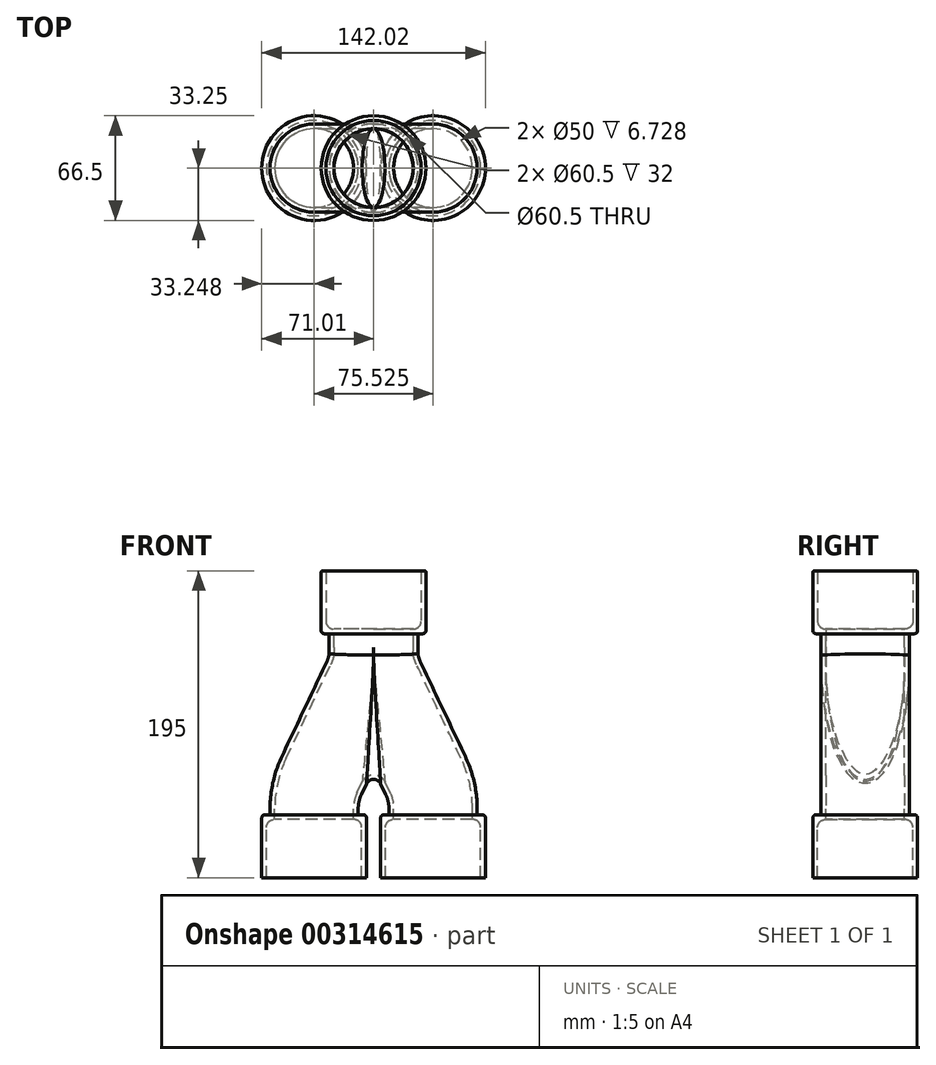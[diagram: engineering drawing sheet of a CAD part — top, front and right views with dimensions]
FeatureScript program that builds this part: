
annotation { "Feature Type Name" : "Feature", "Feature Type Description" : "" }
export const myFeature = defineFeature(function(context is Context, id is Id, definition is map)
    precondition{}
    {
        {
            var Q0;
            Q0=qCreatedBy(makeId("Front.planeOp"),FACE);
            var sketch = newSketch(context, id + "F0", { "sketchPlane" : qUnion([Q0])});
            skLineSegment(sketch, "E0", {"start": v(0, 106.27) * mm, "end": v(0, 115) * mm});
            skLineSegment(sketch, "E1", {"start": v(38, 0) * mm, "end": v(38, 3.73) * mm});
            skLineSegment(sketch, "E2", {"start": v(33.16, 25.18) * mm, "end": v(4.84, 84.82) * mm});
            skPoint(sketch, "E3.visualSharp", {"position": v(38, 15) * mm});
            skArc(sketch, "E3.filletArc", {"start": v(38, 3.73) * mm, "mid": v(36.78, 14.72) * mm, "end": v(33.16, 25.18) * mm});
            skPoint(sketch, "E4.visualSharp", {"position": v(101.3, 16.76) * mm});
            skPoint(sketch, "E5.orphan", {"position": v(0, 0) * mm});
            skPoint(sketch, "E6.visualSharp", {"position": v(0, 95) * mm});
            skArc(sketch, "E6.filletArc", {"start": v(0, 106.27) * mm, "mid": v(1.22, 95.28) * mm, "end": v(4.84, 84.82) * mm});
            skSolve(sketch);
        }
        {
            var Q0;
            Q0=qCreatedBy(makeId("Top.planeOp"),FACE);
            var sketch = newSketch(context, id + "F1", { "sketchPlane" : qUnion([Q0])});
            skCircle(sketch, "E7", {"center": v(37.76, 0) * mm, "radius": 28 * mm});
            skSolve(sketch);
        }
        {
            var Q0;
            Q0=makeQuery(id+"F1.imprint","IMPRINT",FACE,{"disambiguationData":[TD([[makeQuery(id+"F1.imprint","IMPRINT",EDGE,{"derivedFrom":sQuery(id+"F1.wireOp",EDGE,"E7")}),1.0]])]});
            var Q1;
            Q1=sQuery(id+"F0.wireOp",EDGE,"E1");
            var Q2;
            Q2=sQuery(id+"F0.wireOp",EDGE,"E3.filletArc");
            var Q3;
            Q3=sQuery(id+"F0.wireOp",EDGE,"E2");
            var Q4;
            Q4=sQuery(id+"F0.wireOp",EDGE,"E6.filletArc");
            var Q5;
            Q5=sQuery(id+"F0.wireOp",EDGE,"E0");
            sweep(context, id + "F2", {"profiles" : qUnion([Q0]), "path" : qUnion([Q1, Q2, Q3, Q4, Q5])});
        }
        {
            var Q0;
            Q0=makeQuery(id+"F2.opSweep","SWEPT_BODY",BODY,{"disambiguationData":[OSD([sQuery(id+"F0.wireOp",EDGE,"E0"),sQuery(id+"F1.wireOp",EDGE,"E7")])]});
            var Q1;
            Q1=qCreatedBy(makeId("Right.planeOp"),FACE);
            mirror(context, id + "F3", {"entities" : qUnion([Q0]), "mirrorPlane" : qUnion([Q1])});
        }
        {
            var Q0;
            Q0=makeQuery(id+"F3.opPattern","COPY",BODY,{"derivedFrom":makeQuery(id+"F2.opSweep","SWEPT_BODY",BODY,{"disambiguationData":[OSD([sQuery(id+"F0.wireOp",EDGE,"E0"),sQuery(id+"F1.wireOp",EDGE,"E7")])]}),"instanceName":"1"});
            var Q1;
            Q1=makeQuery(id+"F2.opSweep","SWEPT_BODY",BODY,{"disambiguationData":[OSD([sQuery(id+"F0.wireOp",EDGE,"E0"),sQuery(id+"F1.wireOp",EDGE,"E7")])]});
            booleanBodies(context, id + "F4", {"operationType" : BooleanOperationType.UNION, "tools" : qUnion([Q0, Q1])});
        }
        {
            var Q0;
            Q0=qCreatedBy(makeId("Top.planeOp"),FACE);
            var sketch = newSketch(context, id + "F5", { "sketchPlane" : qUnion([Q0])});
            skCircle(sketch, "E8", {"center": v(37.76, 0) * mm, "radius": 33.25 * mm});
            skCircle(sketch, "E9", {"center": v(-37.76, 0) * mm, "radius": 33.25 * mm});
            skSolve(sketch);
        }
        {
            var Q0;
            Q0=makeQuery(id+"F5.imprint","IMPRINT",FACE,{"disambiguationData":[TD([[makeQuery(id+"F5.imprint","IMPRINT",EDGE,{"derivedFrom":sQuery(id+"F5.wireOp",EDGE,"E9")}),1.0]])]});
            var Q1;
            Q1=makeQuery(id+"F5.imprint","IMPRINT",FACE,{"disambiguationData":[TD([[makeQuery(id+"F5.imprint","IMPRINT",EDGE,{"derivedFrom":sQuery(id+"F5.wireOp",EDGE,"E8")}),1.0]])]});
            extrude(context, id + "F6", {"entities" : qUnion([Q0, Q1]), "operationType" : NewBodyOperationType.ADD, "oppositeDirection" : true, "depth" : 40 * mm});
        }
        {
            var Q0;
            Q0=makeQuery(id+"F3.opPattern","COPY",EDGE,{"derivedFrom":makeQuery(id+"F2.opSweep","CAP_EDGE",EDGE,{"disambiguationData":[OSD([sQuery(id+"F0.wireOp",VERTEX,"E1.start"),sQuery(id+"F1.wireOp",EDGE,"E7")])],"isStart":true}),"instanceName":"1"});
            var Q1;
            Q1=makeQuery(id+"F6.opExtrude","CAP_EDGE",EDGE,{"disambiguationData":[OSD([sQuery(id+"F5.wireOp",EDGE,"E9")])],"isStart":true});
            var Q2;
            Q2=makeQuery(id+"F2.opSweep","CAP_EDGE",EDGE,{"disambiguationData":[OSD([sQuery(id+"F0.wireOp",VERTEX,"E1.start"),sQuery(id+"F1.wireOp",EDGE,"E7")])],"isStart":true});
            var Q3;
            Q3=makeQuery(id+"F6.opExtrude","CAP_EDGE",EDGE,{"disambiguationData":[OSD([sQuery(id+"F5.wireOp",EDGE,"E8")])],"isStart":true});
            fillet(context, id + "F7", {"entities" : qUnion([Q0, Q1, Q2, Q3]), "radius" : 2 * mm, "tangentPropagation" : true, "allowEdgeOverflow" : false});
        }
        {
            var Q0;
            {var subQ0=makeQuery(id+"F2.opSweep","CAP_FACE",FACE,{"disambiguationData":[OSD([sQuery(id+"F0.wireOp",VERTEX,"E0.end"),sQuery(id+"F1.wireOp",EDGE,"E7")])],"isStart":false});Q0=makeQuery(id+"F4.opBoolean","MERGE",FACE,{"derivedFrom":[subQ0,makeQuery(id+"F3.opPattern","COPY",FACE,{"derivedFrom":subQ0,"instanceName":"1"})]});}
            var sketch = newSketch(context, id + "F8", { "sketchPlane" : qUnion([Q0])});
            skCircle(sketch, "E10", {"center": v(0, 0) * mm, "radius": 33.25 * mm});
            skSolve(sketch);
        }
        {
            var Q0;
            {var subQ0=makeQuery(id+"F2.opSweep","CAP_EDGE",EDGE,{"disambiguationData":[OSD([sQuery(id+"F0.wireOp",VERTEX,"E0.end"),sQuery(id+"F1.wireOp",EDGE,"E7")])],"isStart":false});Q0=makeQuery(id+"F8.imprint","IMPRINT",FACE,{"disambiguationData":[TD([[makeQuery(id+"F8.imprint","IMPRINT",EDGE,{"derivedFrom":subQ0}),1.0]])]});}
            var Q1;
            Q1=makeQuery(id+"F8.imprint","IMPRINT",FACE,{"disambiguationData":[TD([[makeQuery(id+"F8.imprint","IMPRINT",EDGE,{"derivedFrom":sQuery(id+"F8.wireOp",EDGE,"E10")}),1.0]])]});
            var Q2;
            Q2=sQuery(id+"F8.wireOp",EDGE,"E10");
            extrude(context, id + "F9", {"entities" : qUnion([Q0, Q1]), "operationType" : NewBodyOperationType.ADD, "surfaceEntities" : qUnion([Q2]), "depth" : 40 * mm});
        }
        {
            var Q0;
            Q0=makeQuery(id+"F3.opPattern","COPY",EDGE,{"derivedFrom":makeQuery(id+"F2.opSweep","CAP_EDGE",EDGE,{"disambiguationData":[OSD([sQuery(id+"F0.wireOp",VERTEX,"E0.end"),sQuery(id+"F1.wireOp",EDGE,"E7")])],"isStart":false}),"instanceName":"1"});
            var Q1;
            Q1=makeQuery(id+"F2.opSweep","CAP_EDGE",EDGE,{"disambiguationData":[OSD([sQuery(id+"F0.wireOp",VERTEX,"E0.end"),sQuery(id+"F1.wireOp",EDGE,"E7")])],"isStart":false});
            var Q2;
            Q2=makeQuery(id+"F9.opExtrude","CAP_EDGE",EDGE,{"disambiguationData":[OSD([sQuery(id+"F8.wireOp",EDGE,"E10")])],"isStart":true});
            fillet(context, id + "F10", {"entities" : qUnion([Q0, Q1, Q2]), "radius" : 2 * mm, "tangentPropagation" : true, "allowEdgeOverflow" : false});
        }
        {
            var Q0;
            {var subQ0=makeQuery(id+"F2.opSweep","SWEPT_FACE",FACE,{"disambiguationData":[OSD([sQuery(id+"F0.wireOp",EDGE,"E2"),sQuery(id+"F1.wireOp",EDGE,"E7")])]});Q0=makeQuery(id+"F4.opBoolean","INTERSECT",EDGE,{"derivedFrom":[subQ0,makeQuery(id+"F3.opPattern","COPY",FACE,{"derivedFrom":subQ0,"instanceName":"1"})]});}
            fillet(context, id + "F11", {"entities" : qUnion([Q0]), "radius" : 5 * mm, "tangentPropagation" : true, "allowEdgeOverflow" : false});
        }
        {
            var Q0;
            Q0=makeQuery(id+"F6.opExtrude","CAP_FACE",FACE,{"disambiguationData":[OSD([sQuery(id+"F5.wireOp",EDGE,"E9")])],"isStart":false});
            var Q1;
            Q1=makeQuery(id+"F6.opExtrude","CAP_FACE",FACE,{"disambiguationData":[OSD([sQuery(id+"F5.wireOp",EDGE,"E8")])],"isStart":false});
            var Q2;
            Q2=makeQuery(id+"F9.opExtrude","CAP_FACE",FACE,{"disambiguationData":[OSD([sQuery(id+"F8.wireOp",EDGE,"E10")])],"isStart":false});
            shell(context, id + "F12", {"entities" : qUnion([Q0, Q1, Q2]), "thickness" : 3 * mm});
        }
        {
            var Q0;
            {var subQ0=sQuery(id+"F5.wireOp",EDGE,"E8");var subQ1=makeQuery(id+"F6.opExtrude","CAP_EDGE",EDGE,{"disambiguationData":[OSD([subQ0])],"isStart":true});Q0=makeQuery(id+"F12.opShell","OFFSET_EDGE",EDGE,{"disambiguationData":[OSD([subQ0]),TDD([makeQuery(id+"F7.opFillet","BLEND_EDGE",EDGE,{"blendedFrom":[subQ1,makeQuery(id+"F6.opExtrude","SWEPT_FACE",FACE,{"disambiguationData":[OSD([subQ0])]})],"blendedInto":[makeQuery(id+"F6.opExtrude","SWEPT_FACE",FACE,{"disambiguationData":[OSD([subQ0])]})]}),makeQuery(id+"F7.opFillet","BLEND_EDGE",EDGE,{"blendedFrom":[subQ1,makeQuery(id+"F6.opExtrude","CAP_FACE",FACE,{"disambiguationData":[OSD([subQ0])],"isStart":true})],"blendedInto":[makeQuery(id+"F6.opExtrude","CAP_FACE",FACE,{"disambiguationData":[OSD([subQ0])],"isStart":true})]})])]});}
            var Q1;
            {var subQ0=sQuery(id+"F5.wireOp",EDGE,"E9");var subQ1=makeQuery(id+"F6.opExtrude","CAP_EDGE",EDGE,{"disambiguationData":[OSD([subQ0])],"isStart":true});Q1=makeQuery(id+"F12.opShell","OFFSET_EDGE",EDGE,{"disambiguationData":[OSD([subQ0]),TDD([makeQuery(id+"F7.opFillet","BLEND_EDGE",EDGE,{"blendedFrom":[subQ1,makeQuery(id+"F6.opExtrude","SWEPT_FACE",FACE,{"disambiguationData":[OSD([subQ0])]})],"blendedInto":[makeQuery(id+"F6.opExtrude","SWEPT_FACE",FACE,{"disambiguationData":[OSD([subQ0])]})]}),makeQuery(id+"F7.opFillet","BLEND_EDGE",EDGE,{"blendedFrom":[subQ1,makeQuery(id+"F6.opExtrude","CAP_FACE",FACE,{"disambiguationData":[OSD([subQ0])],"isStart":true})],"blendedInto":[makeQuery(id+"F6.opExtrude","CAP_FACE",FACE,{"disambiguationData":[OSD([subQ0])],"isStart":true})]})])]});}
            var Q2;
            {var subQ0=sQuery(id+"F8.wireOp",EDGE,"E10");var subQ1=makeQuery(id+"F9.opExtrude","CAP_EDGE",EDGE,{"disambiguationData":[OSD([subQ0])],"isStart":true});Q2=makeQuery(id+"F12.opShell","OFFSET_EDGE",EDGE,{"disambiguationData":[OSD([subQ0]),TDD([makeQuery(id+"F10.opFillet","BLEND_EDGE",EDGE,{"blendedFrom":[subQ1,makeQuery(id+"F9.opExtrude","SWEPT_FACE",FACE,{"disambiguationData":[OSD([subQ0])]})],"blendedInto":[makeQuery(id+"F9.opExtrude","SWEPT_FACE",FACE,{"disambiguationData":[OSD([subQ0])]})]}),makeQuery(id+"F10.opFillet","BLEND_EDGE",EDGE,{"blendedFrom":[subQ1,makeQuery(id+"F9.opExtrude","CAP_FACE",FACE,{"disambiguationData":[OSD([subQ0])],"isStart":true})],"blendedInto":[makeQuery(id+"F9.opExtrude","CAP_FACE",FACE,{"disambiguationData":[OSD([subQ0])],"isStart":true})]})])]});}
            fillet(context, id + "F13", {"entities" : qUnion([Q0, Q1, Q2]), "radius" : 5 * mm, "tangentPropagation" : true, "allowEdgeOverflow" : false});
        }
        {
            var Q0;
            Q0=makeQuery(id+"F9.opExtrude","CAP_EDGE",EDGE,{"disambiguationData":[OSD([sQuery(id+"F8.wireOp",EDGE,"E10")])],"isStart":false});
            var Q1;
            {var subQ0=sQuery(id+"F8.wireOp",EDGE,"E10");Q1=makeQuery(id+"F12.opShell","OFFSET_EDGE",EDGE,{"disambiguationData":[OSD([subQ0]),TDD([makeQuery(id+"F9.opExtrude","CAP_EDGE",EDGE,{"disambiguationData":[OSD([subQ0])],"isStart":false})])]});}
            fillet(context, id + "F14", {"entities" : qUnion([Q0, Q1]), "radius" : 1 * mm, "tangentPropagation" : true, "allowEdgeOverflow" : false});
        }
    });
